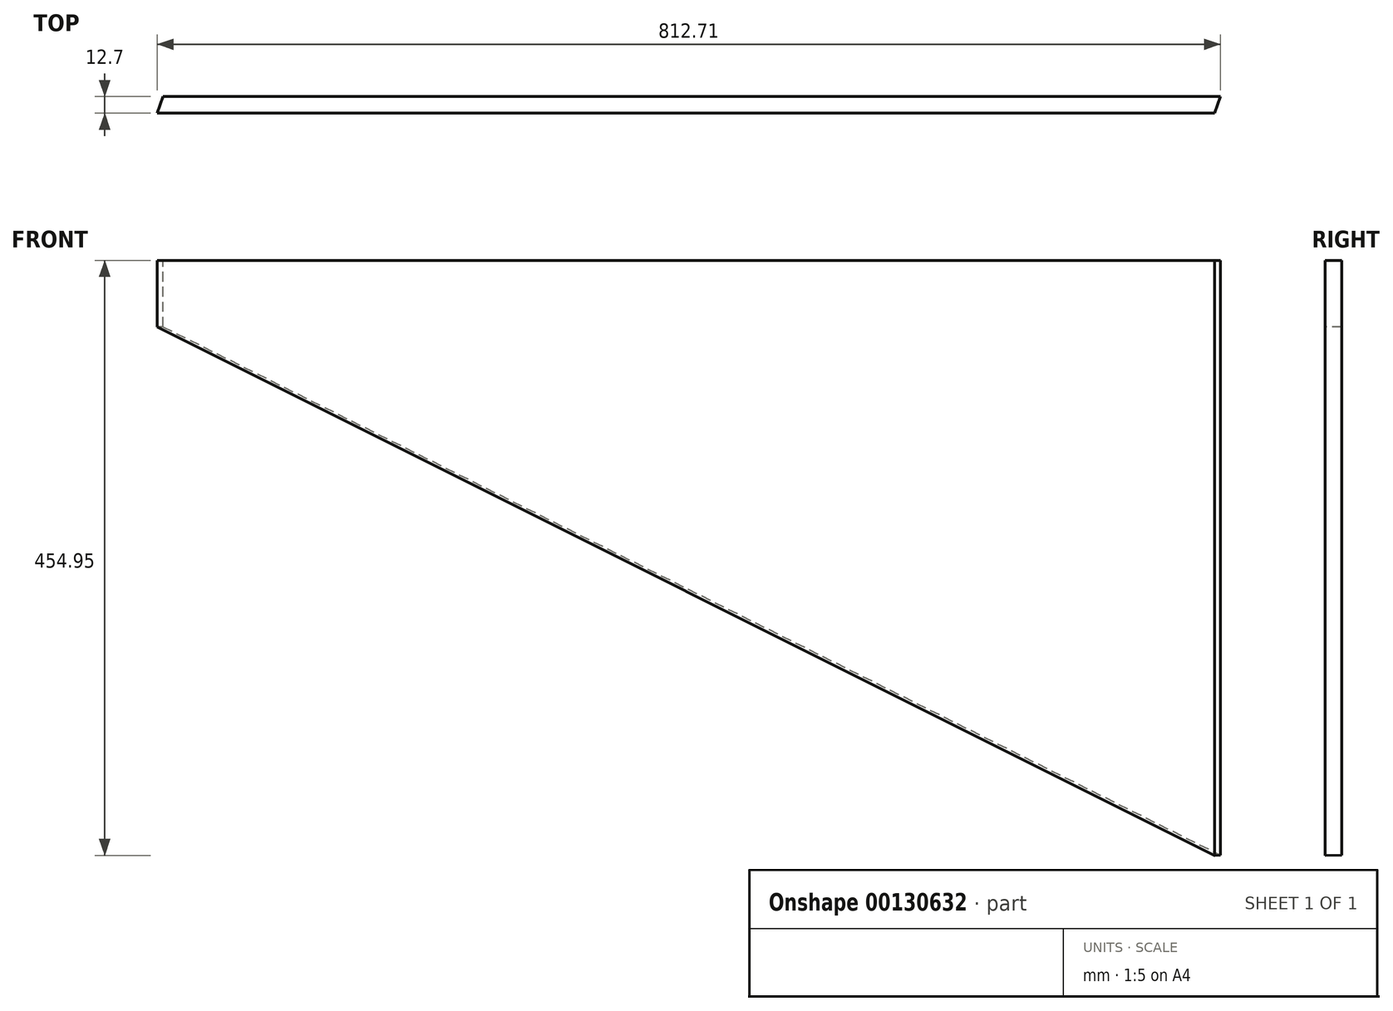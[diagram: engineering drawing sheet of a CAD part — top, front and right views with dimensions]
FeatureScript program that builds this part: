
annotation { "Feature Type Name" : "Feature", "Feature Type Description" : "" }
export const myFeature = defineFeature(function(context is Context, id is Id, definition is map)
    precondition{}
    {
        {
            var Q0;
            Q0=qCreatedBy(makeId("Front.planeOp"),FACE);
            var sketch = newSketch(context, id + "F0", { "sketchPlane" : qUnion([Q0])});
            skLineSegment(sketch, "E0", {"start": v(0, 0) * mm, "end": v(-914.4, 0) * mm});
            skLineSegment(sketch, "E1", {"start": v(-914.4, 0) * mm, "end": v(0, -457.2) * mm});
            skLineSegment(sketch, "E2", {"start": v(0, -457.2) * mm, "end": v(0, 0) * mm});
            skSolve(sketch);
        }
        {
            var Q0;
            Q0=makeQuery(id+"F0.imprint","IMPRINT",FACE,{"disambiguationData":[TD([[makeQuery(id+"F0.imprint","IMPRINT",EDGE,{"derivedFrom":sQuery(id+"F0.wireOp",EDGE,"E0")}),1.0]])]});
            extrude(context, id + "F1", {"entities" : qUnion([Q0]), "depth" : 12.7 * mm});
        }
        {
            var Q0;
            Q0=makeQuery(id+"F1.opExtrude","CAP_FACE",FACE,{"disambiguationData":[OSD([sQuery(id+"F0.wireOp",EDGE,"E0"),sQuery(id+"F0.wireOp",EDGE,"E1"),sQuery(id+"F0.wireOp",EDGE,"E2")])],"isStart":true});
            var sketch = newSketch(context, id + "F2", { "sketchPlane" : qUnion([Q0])});
            skLineSegment(sketch, "E3", {"start": v(0, -457.2) * mm, "end": v(914.4, 0) * mm});
            skLineSegment(sketch, "E4", {"start": v(457.2, -228.6) * mm, "end": v(342.9, 0) * mm});
            skLineSegment(sketch, "E5", {"start": v(342.9, 0) * mm, "end": v(914.4, 0) * mm});
            skSolve(sketch);
        }
        {
            var Q0;
            Q0=sQuery(id+"F2.wireOp",EDGE,"E4");
            cPlane(context, id + "F3", {"entities" : qUnion([Q0]), "cplaneType" : CPlaneType.LINE_ANGLE, "offset" : 25.4 * mm, "angle" : 0 * degree, "width" : 152.4 * mm, "height" : 152.4 * mm});
        }
        {
            var Q0;
            Q0=qCreatedBy(id+"F3.planeOp",FACE);
            var sketch = newSketch(context, id + "F4", { "sketchPlane" : qUnion([Q0])});
            skLineSegment(sketch, "E6", {"start": v(0, -408.93) * mm, "end": v(-12.7, -408.93) * mm});
            skLineSegment(sketch, "E7", {"start": v(-12.7, -408.93) * mm, "end": v(0, -406.84) * mm});
            skLineSegment(sketch, "E8", {"start": v(0, -406.84) * mm, "end": v(0, -408.93) * mm});
            skSolve(sketch);
        }
        {
            var Q0;
            Q0=makeQuery(id+"F4.imprint","IMPRINT",FACE,{"disambiguationData":[TD([[makeQuery(id+"F4.imprint","IMPRINT",EDGE,{"derivedFrom":sQuery(id+"F4.wireOp",EDGE,"E6")}),-1.0]])]});
            extrude(context, id + "F5", {"entities" : qUnion([Q0]), "operationType" : NewBodyOperationType.REMOVE, "endBound" : BoundingType.THROUGH_ALL, "oppositeDirection" : true, "depth" : 25.4 * mm, "hasSecondDirection" : true, "secondDirectionBound" : SecondDirectionBoundingType.THROUGH_ALL, "secondDirectionOppositeDirection" : false, "secondDirectionDepth" : 25.4 * mm});
        }
        {
            var Q0;
            Q0=makeQuery(id+"F1.opExtrude","SWEPT_FACE",FACE,{"disambiguationData":[OSD([sQuery(id+"F0.wireOp",EDGE,"E0")])]});
            var sketch = newSketch(context, id + "F6", { "sketchPlane" : qUnion([Q0])});
            skPoint(sketch, "E9.endSnap0", {"position": v(0, -6.35) * mm});
            skLineSegment(sketch, "E10", {"start": v(0, -6.35) * mm, "end": v(-914.4, -6.35) * mm});
            skLineSegment(sketch, "E11.MirrorCS", {"start": v(-914.4, -300.31) * mm, "end": v(-808.22, 0) * mm});
            skLineSegment(sketch, "E12.MirrorCS", {"start": v(-914.4, 0) * mm, "end": v(-914.4, -300.31) * mm});
            skLineSegment(sketch, "E13.MirrorCS", {"start": v(0, 0) * mm, "end": v(-125.57, -355.17) * mm});
            skLineSegment(sketch, "E14.MirrorCS", {"start": v(0, -355.17) * mm, "end": v(0, 0) * mm});
            skLineSegment(sketch, "E15.MirrorCS", {"start": v(0, 0) * mm, "end": v(-914.4, 0) * mm});
            skLineSegment(sketch, "E16.MirrorCS", {"start": v(-125.57, -355.17) * mm, "end": v(0, -355.17) * mm});
            skSolve(sketch);
        }
        {
            var Q0;
            {var subQ0=sQuery(id+"F6.wireOp",EDGE,"E11.MirrorCS");var subQ5=sQuery(id+"F6.wireOp",EDGE,"E15.MirrorCS");var subQ6=makeQuery(id+"F6.imprint","INTERSECT",VERTEX,{"derivedFrom":[subQ0,subQ5]});Q0=makeQuery(id+"F6.imprint","IMPRINT",FACE,{"disambiguationData":[TD([[makeQuery(id+"F6.imprint","IMPRINT",EDGE,{"disambiguationData":[TD([[subQ6,1.0]])],"derivedFrom":subQ0}),1.0]])]});}
            var Q1;
            {var subQ0=sQuery(id+"F6.wireOp",EDGE,"E11.MirrorCS");var subQ1=sQuery(id+"F6.wireOp",EDGE,"E10");var subQ2=makeQuery(id+"F6.imprint","INTERSECT",VERTEX,{"derivedFrom":[subQ1,subQ0]});Q1=makeQuery(id+"F6.imprint","IMPRINT",FACE,{"disambiguationData":[TD([[makeQuery(id+"F6.imprint","IMPRINT",EDGE,{"disambiguationData":[TD([[subQ2,1.0]])],"derivedFrom":subQ0}),1.0]])]});}
            var Q2;
            {var subQ0=sQuery(id+"F6.wireOp",EDGE,"E14.MirrorCS");var subQ1=sQuery(id+"F6.wireOp",EDGE,"E10");var subQ2=makeQuery(id+"F6.imprint","INTERSECT",VERTEX,{"derivedFrom":[subQ1,subQ0]});Q2=makeQuery(id+"F6.imprint","IMPRINT",FACE,{"disambiguationData":[TD([[makeQuery(id+"F6.imprint","IMPRINT",EDGE,{"disambiguationData":[TD([[subQ2,-1.0]])],"derivedFrom":subQ1}),-1.0]])]});}
            var Q3;
            {var subQ0=sQuery(id+"F6.wireOp",EDGE,"E14.MirrorCS");var subQ1=sQuery(id+"F6.wireOp",EDGE,"E10");var subQ2=makeQuery(id+"F6.imprint","INTERSECT",VERTEX,{"derivedFrom":[subQ1,subQ0]});Q3=makeQuery(id+"F6.imprint","IMPRINT",FACE,{"disambiguationData":[TD([[makeQuery(id+"F6.imprint","IMPRINT",EDGE,{"disambiguationData":[TD([[subQ2,-1.0]])],"derivedFrom":subQ1}),1.0]])]});}
            extrude(context, id + "F7", {"entities" : qUnion([Q0, Q1, Q2, Q3]), "operationType" : NewBodyOperationType.REMOVE, "endBound" : BoundingType.THROUGH_ALL, "oppositeDirection" : true, "depth" : 25.4 * mm});
        }
    });
